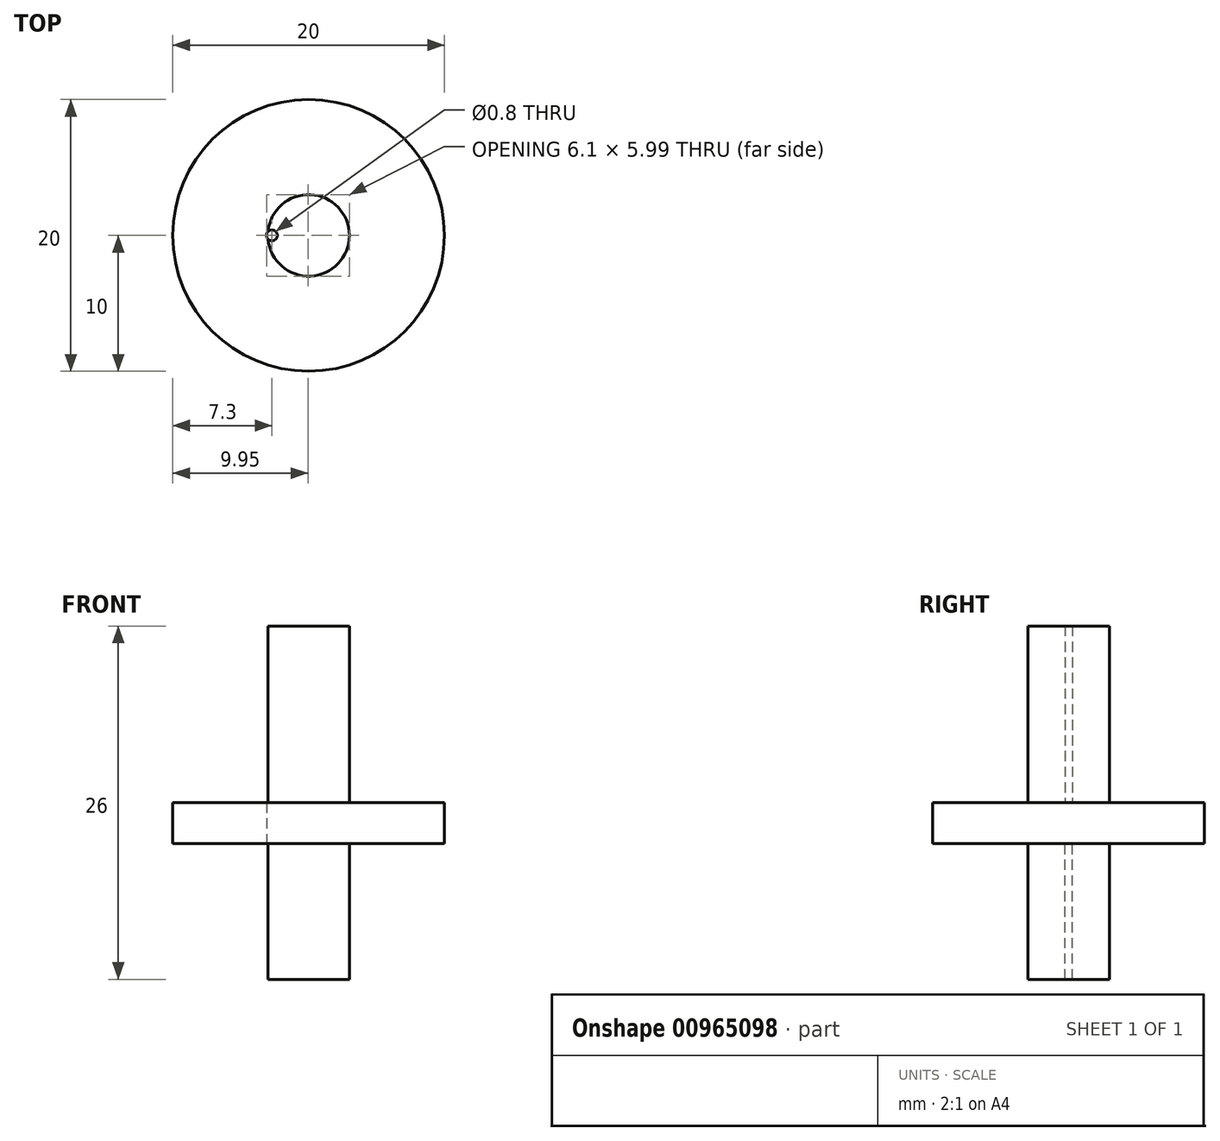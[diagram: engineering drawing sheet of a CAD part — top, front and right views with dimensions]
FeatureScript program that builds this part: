
annotation { "Feature Type Name" : "Feature", "Feature Type Description" : "" }
export const myFeature = defineFeature(function(context is Context, id is Id, definition is map)
    precondition{}
    {
        {
            var Q0;
            Q0=qCreatedBy(makeId("Top.planeOp"),FACE);
            var sketch = newSketch(context, id + "F0", { "sketchPlane" : qUnion([Q0])});
            skCircle(sketch, "E0", {"center": v(0, 0) * mm, "radius": 10 * mm});
            skCircle(sketch, "E1", {"center": v(0, 0) * mm, "radius": 3 * mm});
            skCircle(sketch, "E2", {"center": v(0, 0) * mm, "radius": 1.65 * mm});
            skCircle(sketch, "E3", {"center": v(-2.7, 0) * mm, "radius": 0.4 * mm});
            skSolve(sketch);
        }
        {
            var Q0;
            Q0=makeQuery(id+"F0.imprint","IMPRINT",FACE,{"disambiguationData":[TD([[makeQuery(id+"F0.imprint","IMPRINT",EDGE,{"derivedFrom":sQuery(id+"F0.wireOp",EDGE,"E0")}),1.0]])]});
            extrude(context, id + "F1", {"entities" : qUnion([Q0]), "depth" : 3 * mm, "offsetDistance" : 25 * mm});
        }
        {
            var Q0;
            Q0=makeQuery(id+"F0.imprint","IMPRINT",FACE,{"disambiguationData":[TD([[makeQuery(id+"F0.imprint","IMPRINT",EDGE,{"derivedFrom":sQuery(id+"F0.wireOp",EDGE,"E2")}),-1.0]])]});
            var Q1;
            Q1=makeQuery(id+"F0.imprint","IMPRINT",FACE,{"disambiguationData":[TD([[makeQuery(id+"F0.imprint","IMPRINT",EDGE,{"derivedFrom":sQuery(id+"F0.wireOp",EDGE,"E2")}),1.0]])]});
            extrude(context, id + "F2", {"entities" : qUnion([Q0, Q1]), "operationType" : NewBodyOperationType.ADD, "depth" : 16 * mm, "offsetDistance" : 25 * mm});
        }
        {
            var Q0;
            Q0=makeQuery(id+"F0.imprint","IMPRINT",FACE,{"disambiguationData":[TD([[makeQuery(id+"F0.imprint","IMPRINT",EDGE,{"derivedFrom":sQuery(id+"F0.wireOp",EDGE,"E2")}),-1.0]])]});
            var Q1;
            Q1=makeQuery(id+"F0.imprint","IMPRINT",FACE,{"disambiguationData":[TD([[makeQuery(id+"F0.imprint","IMPRINT",EDGE,{"derivedFrom":sQuery(id+"F0.wireOp",EDGE,"E2")}),1.0]])]});
            extrude(context, id + "F3", {"entities" : qUnion([Q0, Q1]), "operationType" : NewBodyOperationType.ADD, "oppositeDirection" : true, "depth" : 10 * mm, "offsetDistance" : 25 * mm});
        }
    });
